# Revit family: Domotics-DomesticRanges-GEWISS-CHORUS_POWER-SOCKET-OUTLET_MULTISTANDARD
name_source: partatom
category: Apparecchi elettrici
revit_build: Autodesk Revit 2016 (Build: 20161004_0715(x64)
units: mm (PartAtom-declared; Revit-internal decimal feet)

## family parameters
Condiviso = Sì
Host = Superficie
Mantenere orientamento annotazione = Sì
Punto di calcolo locali = Sì
Quota connettore circolare = Usa diametro
Taglio con vuoti quando caricato = Sì
Tipo di parte = Normale

## types (3) — shared parameters
Carico apparente = 0 VA
Catalogue = DOMOTICS
Catalogue Range = CHORUS - DOMESTIC RANGE
Electrocod = 0131
IDF = c8cb9e08-9141-46ff-9284-b9ac4634f669
IDT = ac5b5f1b-473c-47f8-aca9-a946d0340a4d
Immagine tipo = GW14310.jpg
N. poli = 2
Produttore = GEWISS S.p.A.
Prospetto di default = 1219 mm
TXT ELETTRICO = 15
Technical sheet = https://www.gewiss.com
Tipo_ = CHORUS PRESE INDIA SUDAFRICA_GENERICO : TITANIO
URL = https://www.gewiss.com
Version file RFA = 19.0
Volt = 230 V

## per-type parameters (varying)
| type | Descrizione | EAN code | Modello |
| GW14310 - MULTISTANDARD SOCKET OUTLET TITANIUM | MULTISTANDARD SOCKET OUTLET TITANIUM | 8011564795044 | GW14310 |
| GW10310 - MULTISTANDARD SOCKET OUTLET WHITE | MULTISTANDARD SOCKET OUTLET WHITE | 8011564795020 | GW10310 |
| GW12310 - MULTISTANDARD SOCKET OUTLET BLACK | MULTISTANDARD SOCKET OUTLET BLACK | 8011564795037 | GW12310 |

## geometry (parser evidence)
native form markers: Sweep x1
no freeform markers — native parametric forms only
